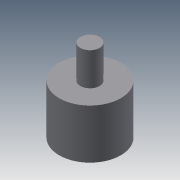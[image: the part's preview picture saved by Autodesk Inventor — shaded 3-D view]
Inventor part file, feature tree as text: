
AUTODESK INVENTOR PART (.ipt)
format: ipt  version: 2013 (Build 170138000, 138)  size: 87,040 bytes
history: native  units: mm
features: sketch x3, extrude x2, plane x1, hole x1
ambient origin geometry x8: Origin, YZ Plane, XZ Plane, XY Plane, X Axis, Y Axis, Z Axis, Center Point
bodies: Solid1 (feature_tree)
feature tree (7):
  extrude  "Extrusion1"  Depth=9.0mm TaperAngle=0.0deg
  plane  "Work Plane1"
  hole  "Hole1"  [1 undecoded]
  extrude  "Extrusion3"  Depth=6.0mm TaperAngle=0.0deg
  sketch  "Sketch1"  dims[d0=11.2mm d1=9.0mm d2=0.0mm]
  sketch  "Sketch3"  dims[d9=2.4mm]
  sketch  "Sketch4"  dims[d10=2.459mm d11=5.6mm d12=4.0mm d13=2.0mm d14=90.0deg d15=5.6mm d16=0.0mm d17=3.5mm d18=6.0mm d19=0.0mm]
note: 1 required parameter value undecoded (feature->parameter linkage not recoverable at this tier; creation-order binding heuristic only, values carry confidence <= 0.55)
